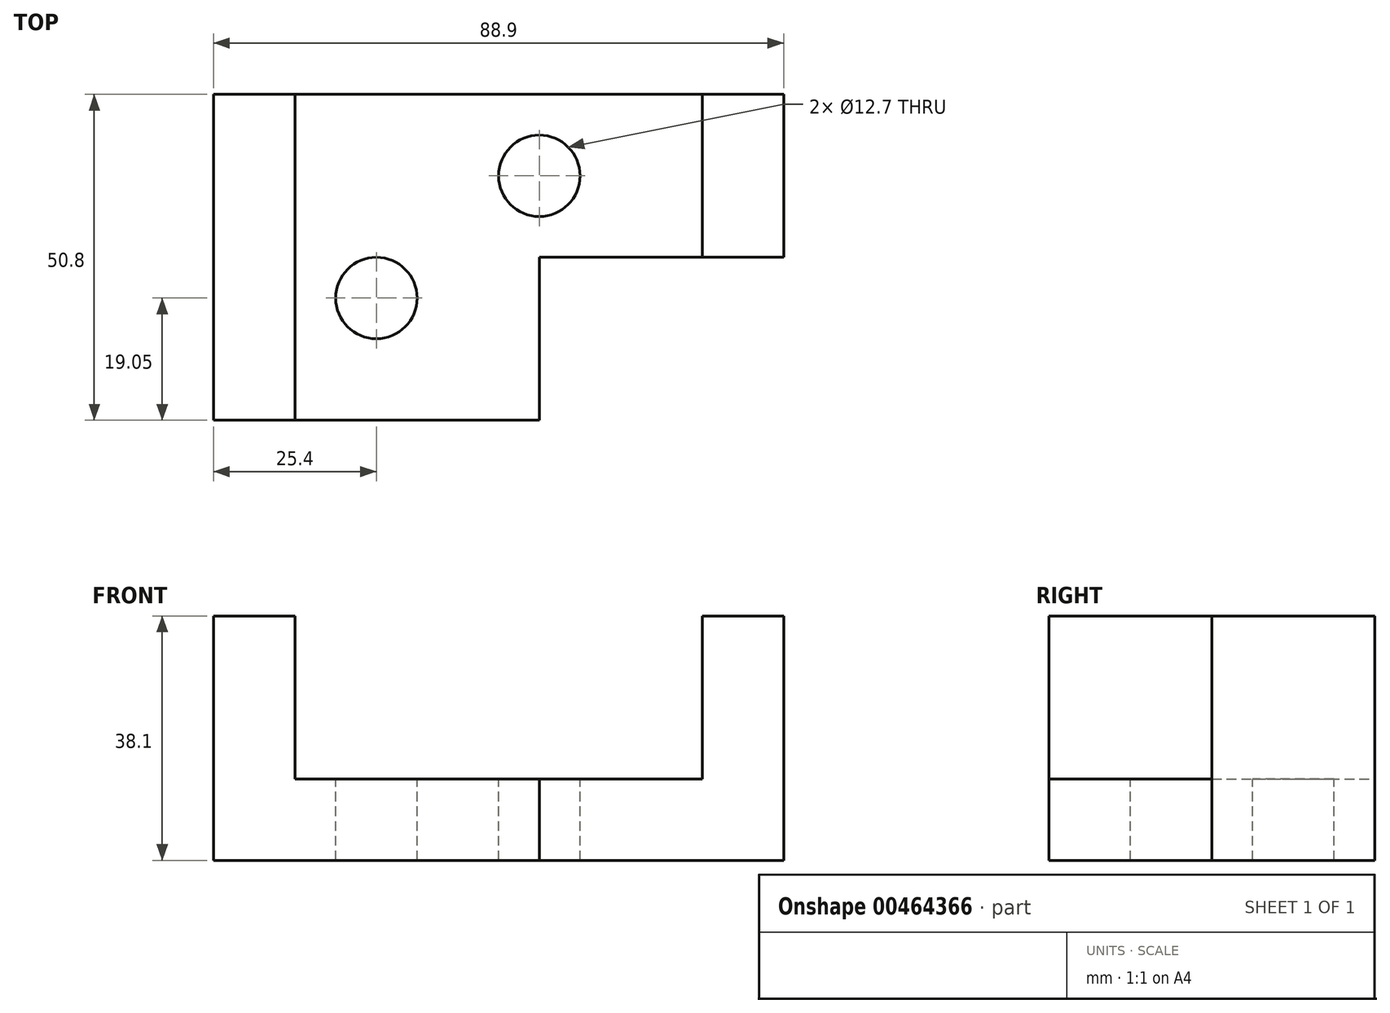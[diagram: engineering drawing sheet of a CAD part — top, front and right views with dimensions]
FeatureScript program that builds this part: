
annotation { "Feature Type Name" : "Feature", "Feature Type Description" : "" }
export const myFeature = defineFeature(function(context is Context, id is Id, definition is map)
    precondition{}
    {
        {
            var Q0;
            Q0=qCreatedBy(makeId("Front.planeOp"),FACE);
            var sketch = newSketch(context, id + "F0", { "sketchPlane" : qUnion([Q0])});
            skLineSegment(sketch, "E0.bottom", {"start": v(-44.45, 19.05) * mm, "end": v(44.45, 19.05) * mm});
            skLineSegment(sketch, "E0.top", {"start": v(-44.45, -19.05) * mm, "end": v(44.45, -19.05) * mm});
            skLineSegment(sketch, "E0.left", {"start": v(-44.45, 19.05) * mm, "end": v(-44.45, -19.05) * mm});
            skLineSegment(sketch, "E0.right", {"start": v(44.45, 19.05) * mm, "end": v(44.45, -19.05) * mm});
            skPoint(sketch, "E0.middle", {"position": v(0, 0) * mm});
            skSolve(sketch);
        }
        {
            var Q0;
            Q0 = qSketchRegion(id + "F0", true);
            extrude(context, id + "F1", {"entities" : qUnion([Q0]), "depth" : 50.8 * mm});
        }
        {
            var Q0;
            Q0=makeQuery(id+"F1.opExtrude","SWEPT_FACE",FACE,{"disambiguationData":[OSD([sQuery(id+"F0.wireOp",EDGE,"E0.bottom")])]});
            var sketch = newSketch(context, id + "F2", { "sketchPlane" : qUnion([Q0])});
            skLineSegment(sketch, "E1.bottom", {"start": v(-31.75, -50.8) * mm, "end": v(31.75, -50.8) * mm});
            skLineSegment(sketch, "E1.top", {"start": v(-31.75, 0) * mm, "end": v(31.75, 0) * mm});
            skLineSegment(sketch, "E1.left", {"start": v(-31.75, -50.8) * mm, "end": v(-31.75, 0) * mm});
            skLineSegment(sketch, "E1.right", {"start": v(31.75, -50.8) * mm, "end": v(31.75, 0) * mm});
            skPoint(sketch, "E1.middle", {"position": v(0, -25.4) * mm});
            skSolve(sketch);
        }
        {
            var Q0;
            Q0 = qSketchRegion(id + "F2", true);
            extrude(context, id + "F3", {"entities" : qUnion([Q0]), "operationType" : NewBodyOperationType.REMOVE, "oppositeDirection" : true, "depth" : 25.4 * mm});
        }
        {
            var Q0;
            Q0=makeQuery(id+"F1.opExtrude","SWEPT_FACE",FACE,{"disambiguationData":[OSD([sQuery(id+"F0.wireOp",EDGE,"E0.right")])]});
            var sketch = newSketch(context, id + "F4", { "sketchPlane" : qUnion([Q0])});
            skLineSegment(sketch, "E2.bottom", {"start": v(-50.8, 19.05) * mm, "end": v(-25.4, 19.05) * mm});
            skLineSegment(sketch, "E2.top", {"start": v(-50.8, -19.05) * mm, "end": v(-25.4, -19.05) * mm});
            skLineSegment(sketch, "E2.left", {"start": v(-50.8, 19.05) * mm, "end": v(-50.8, -19.05) * mm});
            skLineSegment(sketch, "E2.right", {"start": v(-25.4, 19.05) * mm, "end": v(-25.4, -19.05) * mm});
            skSolve(sketch);
        }
        {
            var Q0;
            Q0 = qSketchRegion(id + "F4", true);
            extrude(context, id + "F5", {"entities" : qUnion([Q0]), "operationType" : NewBodyOperationType.REMOVE, "oppositeDirection" : true, "depth" : 38.1 * mm});
        }
        {
            var Q0;
            Q0=makeQuery(id+"F3.boolean.opBoolean","COPY",FACE,{"derivedFrom":makeQuery(id+"F3.opExtrude","CAP_FACE",FACE,{"disambiguationData":[OSD([sQuery(id+"F2.wireOp",EDGE,"E1.bottom"),sQuery(id+"F2.wireOp",EDGE,"E1.top"),sQuery(id+"F2.wireOp",EDGE,"E1.left"),sQuery(id+"F2.wireOp",EDGE,"E1.right")])],"isStart":false})});
            var sketch = newSketch(context, id + "F6", { "sketchPlane" : qUnion([Q0])});
            skCircle(sketch, "E3", {"center": v(-19.05, -31.75) * mm, "radius": 6.35 * mm});
            skCircle(sketch, "E4", {"center": v(6.35, -12.7) * mm, "radius": 6.35 * mm});
            skSolve(sketch);
        }
        {
            var Q0;
            Q0 = qSketchRegion(id + "F6", true);
            extrude(context, id + "F7", {"entities" : qUnion([Q0]), "operationType" : NewBodyOperationType.REMOVE, "oppositeDirection" : true, "depth" : 25.4 * mm});
        }
    });
